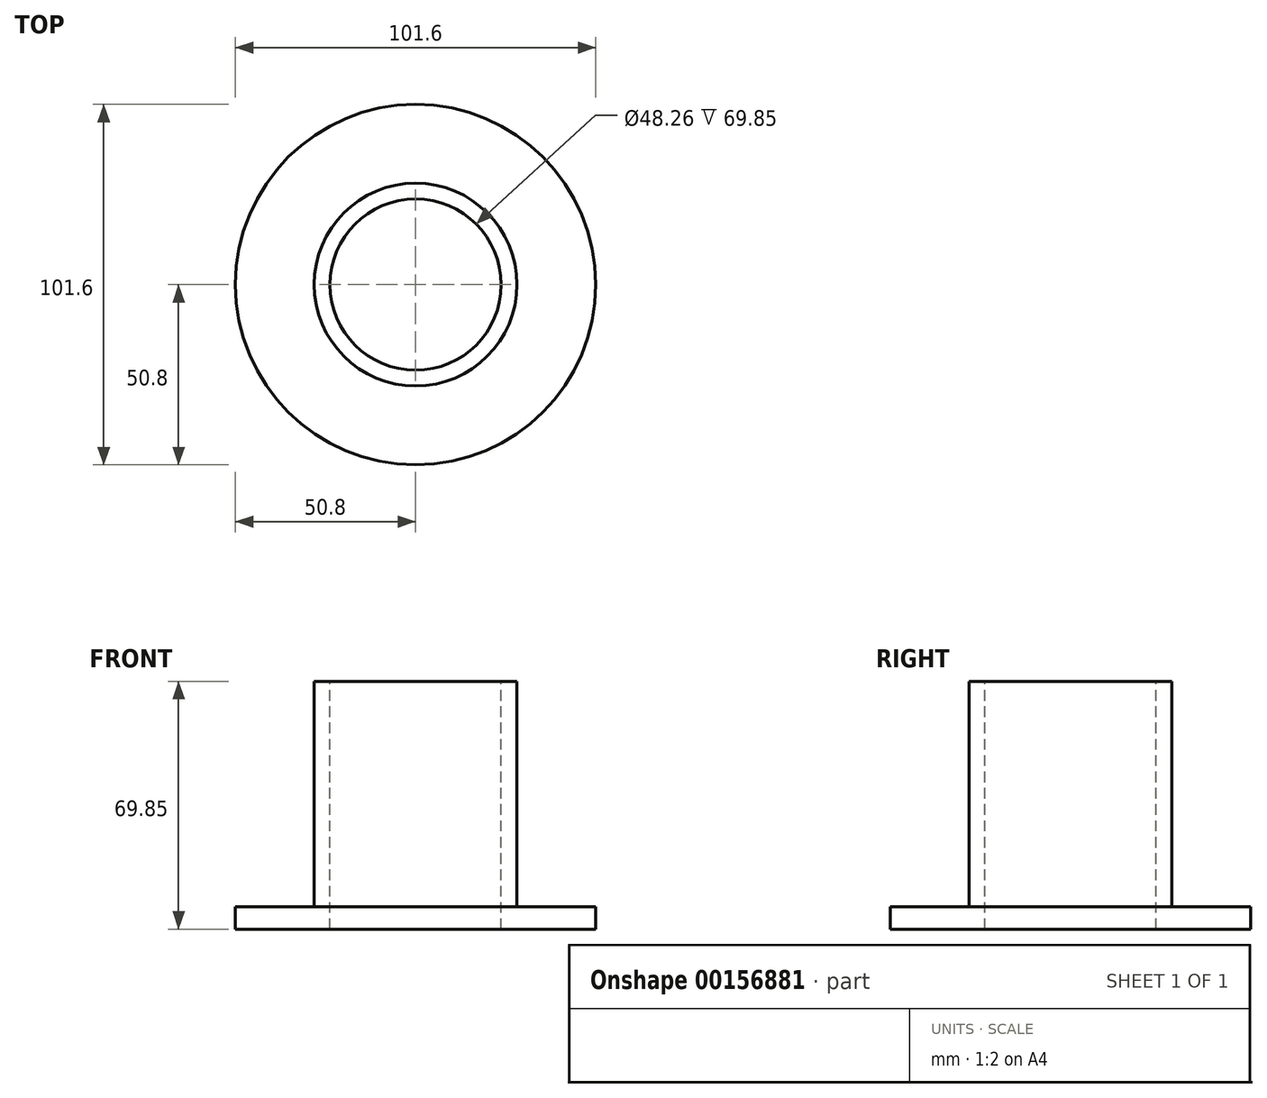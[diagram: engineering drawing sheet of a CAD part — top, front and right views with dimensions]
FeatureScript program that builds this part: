
annotation { "Feature Type Name" : "Feature", "Feature Type Description" : "" }
export const myFeature = defineFeature(function(context is Context, id is Id, definition is map)
    precondition{}
    {
        {
            var Q0;
            Q0=qCreatedBy(makeId("Front.planeOp"),FACE);
            var sketch = newSketch(context, id + "F0", { "sketchPlane" : qUnion([Q0])});
            skLineSegment(sketch, "E0.bottom", {"start": v(24.13, 69.85) * mm, "end": v(28.58, 69.85) * mm});
            skLineSegment(sketch, "E0.left", {"start": v(24.13, 69.85) * mm, "end": v(24.13, 0) * mm});
            skLineSegment(sketch, "E0.right", {"start": v(28.58, 69.85) * mm, "end": v(28.58, 6.35) * mm});
            skLineSegment(sketch, "E1.bottom", {"start": v(28.58, 6.35) * mm, "end": v(50.8, 6.35) * mm});
            skLineSegment(sketch, "E1.top", {"start": v(24.13, 0) * mm, "end": v(50.8, 0) * mm});
            skLineSegment(sketch, "E1.right", {"start": v(50.8, 6.35) * mm, "end": v(50.8, 0) * mm});
            skLineSegment(sketch, "E2", {"start": v(0, 78.8) * mm, "end": v(0, -18.68) * mm, "construction": true});
            skSolve(sketch);
        }
        {
            var Q0;
            Q0=makeQuery(id+"F0.imprint","IMPRINT",FACE,{"disambiguationData":[TD([[makeQuery(id+"F0.imprint","IMPRINT",EDGE,{"derivedFrom":sQuery(id+"F0.wireOp",EDGE,"E0.bottom")}),-1.0]])]});
            var Q1;
            Q1=sQuery(id+"F0.wireOp",EDGE,"E2");
            revolve(context, id + "F1", {"entities" : qUnion([Q0]), "axis" : qUnion([Q1]), "revolveType" : RevolveType.FULL});
        }
    });
